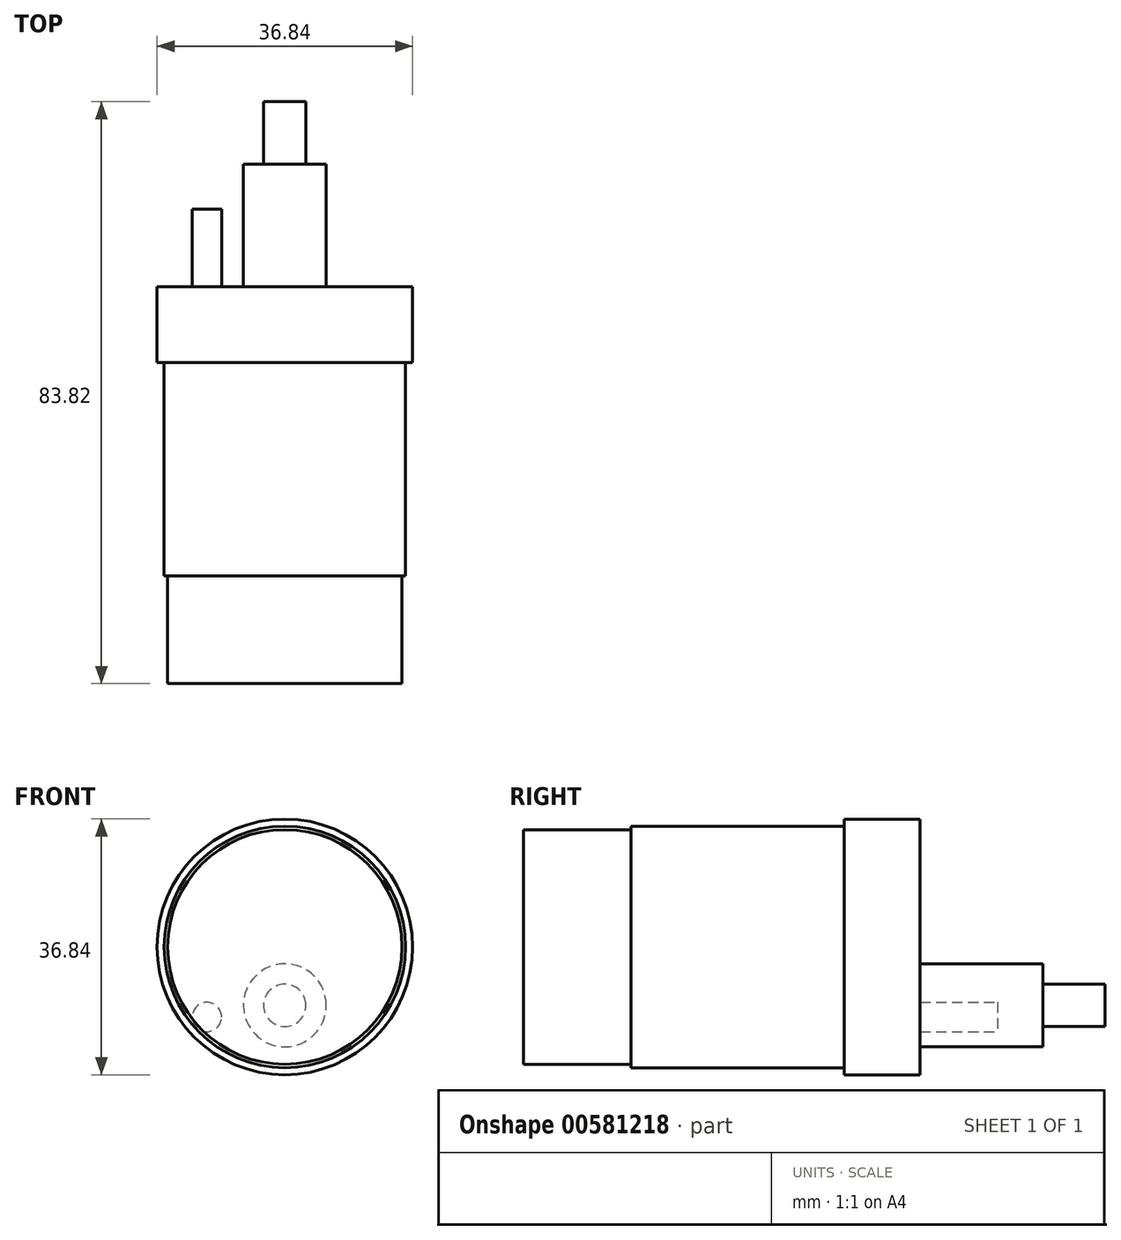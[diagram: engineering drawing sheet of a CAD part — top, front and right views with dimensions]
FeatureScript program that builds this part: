
annotation { "Feature Type Name" : "Feature", "Feature Type Description" : "" }
export const myFeature = defineFeature(function(context is Context, id is Id, definition is map)
    precondition{}
    {
        {
            var Q0;
            Q0=qCreatedBy(makeId("Front.planeOp"),FACE);
            var sketch = newSketch(context, id + "F0", { "sketchPlane" : qUnion([Q0])});
            skCircle(sketch, "E0", {"center": v(0, 0) * mm, "radius": 18.41 * mm});
            skSolve(sketch);
        }
        {
            var Q0;
            Q0=makeQuery(id+"F0.imprint","IMPRINT",FACE,{"disambiguationData":[TD([[makeQuery(id+"F0.imprint","IMPRINT",EDGE,{"derivedFrom":sQuery(id+"F0.wireOp",EDGE,"E0")}),1.0]])]});
            extrude(context, id + "F1", {"entities" : qUnion([Q0]), "depth" : 22.1 * mm, "offsetDistance" : 25.4 * mm});
        }
        {
            var Q0;
            Q0=makeQuery(id+"F1.opExtrude","CAP_FACE",FACE,{"disambiguationData":[OSD([sQuery(id+"F0.wireOp",EDGE,"E0")])],"isStart":true});
            var sketch = newSketch(context, id + "F2", { "sketchPlane" : qUnion([Q0])});
            skCircle(sketch, "E1", {"center": v(0, -8.41) * mm, "radius": 5.97 * mm});
            skCircle(sketch, "E2", {"center": v(0, -8.41) * mm, "radius": 3.05 * mm});
            skSolve(sketch);
        }
        {
            var Q0;
            Q0=makeQuery(id+"F2.imprint","IMPRINT",FACE,{"disambiguationData":[TD([[makeQuery(id+"F2.imprint","IMPRINT",EDGE,{"derivedFrom":sQuery(id+"F2.wireOp",EDGE,"E1")}),1.0]])]});
            extrude(context, id + "F3", {"entities" : qUnion([Q0]), "operationType" : NewBodyOperationType.ADD, "depth" : 6.5 * mm, "offsetDistance" : 25.4 * mm});
        }
        {
            var Q0;
            Q0=makeQuery(id+"F3.boolean.opBoolean","SPLIT",FACE,{"disambiguationData":[TD([makeQuery(id+"F3.opExtrude","SWEPT_FACE",FACE,{"disambiguationData":[OSD([sQuery(id+"F2.wireOp",EDGE,"E2")])]})])],"derivedFrom":makeQuery(id+"F1.opExtrude","CAP_FACE",FACE,{"disambiguationData":[OSD([sQuery(id+"F0.wireOp",EDGE,"E0")])],"isStart":true})});
            extrude(context, id + "F4", {"entities" : qUnion([Q0]), "operationType" : NewBodyOperationType.ADD, "depth" : 15.5 * mm, "offsetDistance" : 25.4 * mm});
        }
        {
            var Q0;
            Q0=makeQuery(id+"F1.opExtrude","CAP_FACE",FACE,{"disambiguationData":[OSD([sQuery(id+"F0.wireOp",EDGE,"E0")])],"isStart":false});
            var sketch = newSketch(context, id + "F5", { "sketchPlane" : qUnion([Q0])});
            skCircle(sketch, "E3", {"center": v(0, 0) * mm, "radius": 17.4 * mm});
            skSolve(sketch);
        }
        {
            var Q0;
            Q0=makeQuery(id+"F5.imprint","IMPRINT",FACE,{"disambiguationData":[TD([[makeQuery(id+"F5.imprint","IMPRINT",EDGE,{"derivedFrom":sQuery(id+"F5.wireOp",EDGE,"E3")}),1.0]])]});
            extrude(context, id + "F6", {"entities" : qUnion([Q0]), "operationType" : NewBodyOperationType.ADD, "depth" : 30.73 * mm, "offsetDistance" : 25.4 * mm});
        }
        {
            var Q0;
            Q0=makeQuery(id+"F6.opExtrude","CAP_FACE",FACE,{"disambiguationData":[OSD([sQuery(id+"F5.wireOp",EDGE,"E3")])],"isStart":false});
            var sketch = newSketch(context, id + "F7", { "sketchPlane" : qUnion([Q0])});
            skCircle(sketch, "E4", {"center": v(0, 0) * mm, "radius": 16.9 * mm});
            skSolve(sketch);
        }
        {
            var Q0;
            Q0=makeQuery(id+"F7.imprint","IMPRINT",FACE,{"disambiguationData":[TD([[makeQuery(id+"F7.imprint","IMPRINT",EDGE,{"derivedFrom":sQuery(id+"F7.wireOp",EDGE,"E4")}),1.0]])]});
            extrude(context, id + "F8", {"entities" : qUnion([Q0]), "operationType" : NewBodyOperationType.ADD, "depth" : 15.5 * mm, "offsetDistance" : 25.4 * mm});
        }
        {
            var Q0;
            {var subQ0=sQuery(id+"F0.wireOp",EDGE,"E0");Q0=makeQuery(id+"F3.boolean.opBoolean","SPLIT",FACE,{"disambiguationData":[TD([makeQuery(id+"F1.opExtrude","SWEPT_FACE",FACE,{"disambiguationData":[OSD([subQ0])]})])],"derivedFrom":makeQuery(id+"F1.opExtrude","CAP_FACE",FACE,{"disambiguationData":[OSD([subQ0])],"isStart":true})});}
            var sketch = newSketch(context, id + "F9", { "sketchPlane" : qUnion([Q0])});
            skCircle(sketch, "E5", {"center": v(0, 15.88) * mm, "radius": 2.11 * mm});
            skCircle(sketch, "E6", {"center": v(-11.23, -10.1) * mm, "radius": 2.12 * mm});
            skLineSegment(sketch, "E7", {"start": v(0, -18.41) * mm, "end": v(0, 17.99) * mm, "construction": true});
            skCircle(sketch, "E8.MirrorC", {"center": v(11.23, -10.1) * mm, "radius": 2.12 * mm});
            skSolve(sketch);
        }
        {
            var Q0;
            Q0=makeQuery(id+"F9.imprint","IMPRINT",FACE,{"disambiguationData":[TD([[makeQuery(id+"F9.imprint","IMPRINT",EDGE,{"derivedFrom":sQuery(id+"F9.wireOp",EDGE,"E6")}),1.0]])]});
            var Q1;
            Q1=makeQuery(id+"F9.imprint","IMPRINT",FACE,{"disambiguationData":[TD([[makeQuery(id+"F9.imprint","IMPRINT",EDGE,{"derivedFrom":sQuery(id+"F9.wireOp",EDGE,"E5")}),1.0]])]});
            var Q2;
            Q2=makeQuery(id+"F9.imprint","IMPRINT",FACE,{"disambiguationData":[TD([[makeQuery(id+"F9.imprint","IMPRINT",EDGE,{"derivedFrom":sQuery(id+"F9.wireOp",EDGE,"E8.MirrorC")}),-1.0]])]});
            extrude(context, id + "F10", {"entities" : qUnion([Q0, Q1, Q2]), "operationType" : NewBodyOperationType.REMOVE, "oppositeDirection" : true, "depth" : 11.18 * mm, "offsetDistance" : 25.4 * mm});
        }
    });
